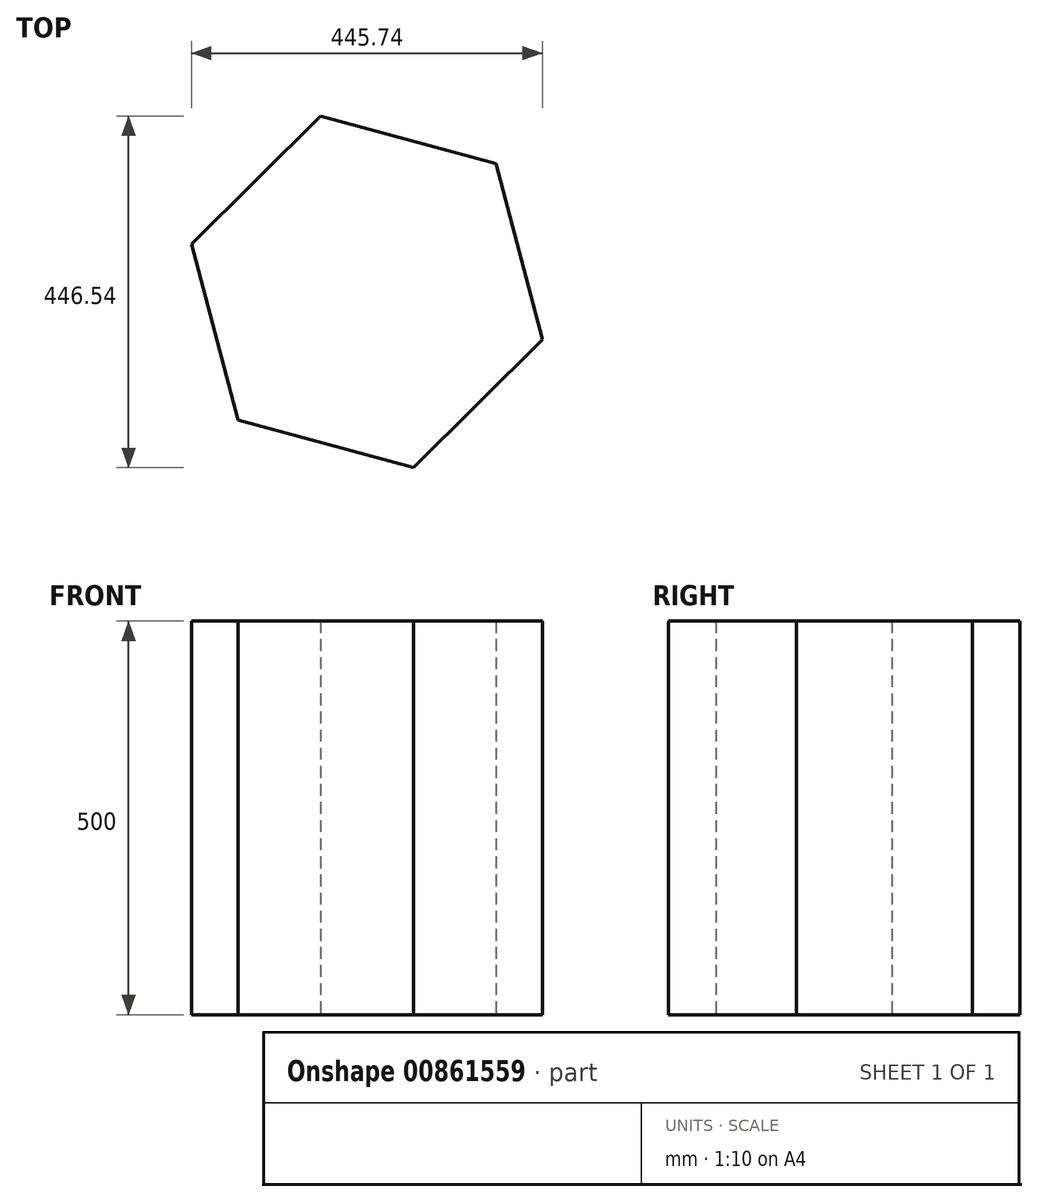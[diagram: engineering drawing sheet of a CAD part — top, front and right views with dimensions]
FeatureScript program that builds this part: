
annotation { "Feature Type Name" : "Feature", "Feature Type Description" : "" }
export const myFeature = defineFeature(function(context is Context, id is Id, definition is map)
    precondition{}
    {
        {
            var Q0;
            Q0=qCreatedBy(makeId("Top.planeOp"),FACE);
            var sketch = newSketch(context, id + "F0", { "sketchPlane" : qUnion([Q0])});
            skCircle(sketch, "E0.cCircle", {"center": v(0, 0) * mm, "radius": 200 * mm, "construction": true});
            skLineSegment(sketch, "E0.0", {"start": v(-59.02, 223.27) * mm, "end": v(163.85, 162.75) * mm});
            skLineSegment(sketch, "E0.1", {"start": v(163.85, 162.75) * mm, "end": v(222.87, -60.52) * mm});
            skLineSegment(sketch, "E0.2", {"start": v(222.87, -60.52) * mm, "end": v(59.02, -223.27) * mm});
            skLineSegment(sketch, "E0.3", {"start": v(59.02, -223.27) * mm, "end": v(-163.85, -162.75) * mm});
            skLineSegment(sketch, "E0.4", {"start": v(-163.85, -162.75) * mm, "end": v(-222.87, 60.52) * mm});
            skLineSegment(sketch, "E0.5", {"start": v(-222.87, 60.52) * mm, "end": v(-59.02, 223.27) * mm});
            skPoint(sketch, "E0.0.midPoint", {"position": v(52.41, 193) * mm});
            skSolve(sketch);
        }
        {
            var Q0;
            Q0=makeQuery(id+"F0.imprint","IMPRINT",FACE,{"disambiguationData":[TD([[makeQuery(id+"F0.imprint","IMPRINT",EDGE,{"derivedFrom":sQuery(id+"F0.wireOp",EDGE,"E0.0")}),-1.0]])]});
            extrude(context, id + "F1", {"entities" : qUnion([Q0]), "depth" : 500 * mm, "offsetDistance" : 25 * mm});
        }
    });
